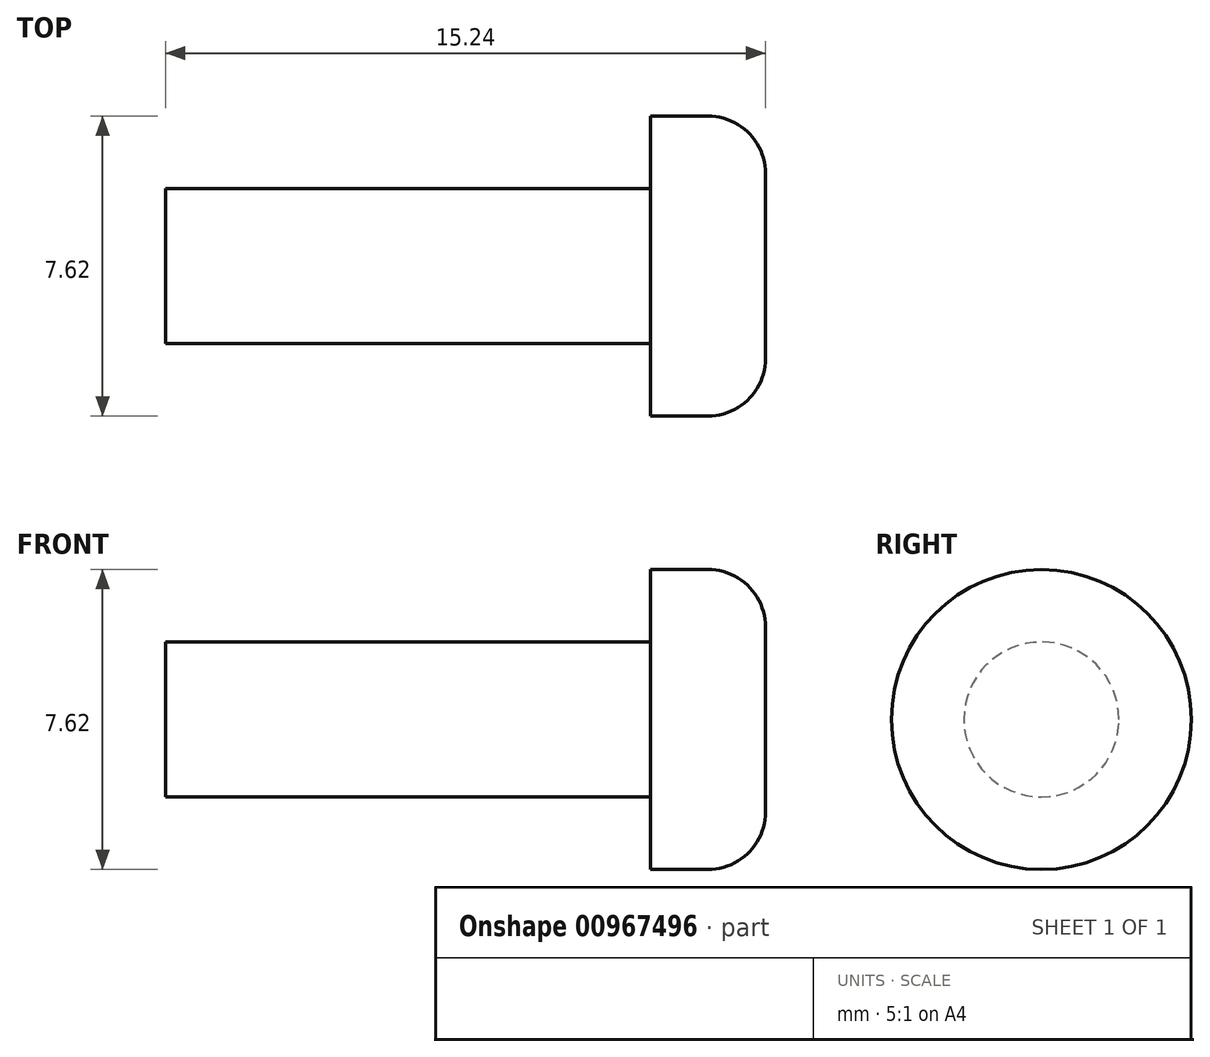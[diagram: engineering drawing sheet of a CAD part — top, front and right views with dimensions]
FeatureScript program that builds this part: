
annotation { "Feature Type Name" : "Feature", "Feature Type Description" : "" }
export const myFeature = defineFeature(function(context is Context, id is Id, definition is map)
    precondition{}
    {
        {
            var Q0;
            Q0=qCreatedBy(makeId("Right.planeOp"),FACE);
            var sketch = newSketch(context, id + "F0", { "sketchPlane" : qUnion([Q0])});
            skCircle(sketch, "E0", {"center": v(0, 0) * mm, "radius": 3.81 * mm});
            skSolve(sketch);
        }
        {
            var Q0;
            Q0 = qSketchRegion(id + "F0", true);
            extrude(context, id + "F1", {"entities" : qUnion([Q0]), "oppositeDirection" : true, "depth" : 2.92 * mm, "offsetDistance" : 25.4 * mm});
        }
        {
            var Q0;
            Q0=makeQuery(id+"F1.opExtrude","CAP_EDGE",EDGE,{"disambiguationData":[OSD([sQuery(id+"F0.wireOp",EDGE,"E0")])],"isStart":true});
            fillet(context, id + "F2", {"entities" : qUnion([Q0]), "radius" : 1.46 * mm, "tangentPropagation" : true, "allowEdgeOverflow" : false});
        }
        {
            var Q0;
            Q0=makeQuery(id+"F1.opExtrude","CAP_FACE",FACE,{"disambiguationData":[OSD([sQuery(id+"F0.wireOp",EDGE,"E0")])],"isStart":false});
            var sketch = newSketch(context, id + "F3", { "sketchPlane" : qUnion([Q0])});
            skCircle(sketch, "E1", {"center": v(0, 0) * mm, "radius": 1.97 * mm});
            skSolve(sketch);
        }
        {
            var Q0;
            Q0=makeQuery(id+"F3.imprint","IMPRINT",FACE,{"disambiguationData":[TD([[makeQuery(id+"F3.imprint","IMPRINT",EDGE,{"derivedFrom":sQuery(id+"F3.wireOp",EDGE,"E1")}),1.0]])]});
            var Q1;
            Q1=sQuery(id+"F3.wireOp",EDGE,"E1");
            extrude(context, id + "F4", {"entities" : qUnion([Q0]), "operationType" : NewBodyOperationType.ADD, "surfaceEntities" : qUnion([Q1]), "depth" : 12.32 * mm, "offsetDistance" : 25.4 * mm});
        }
    });
